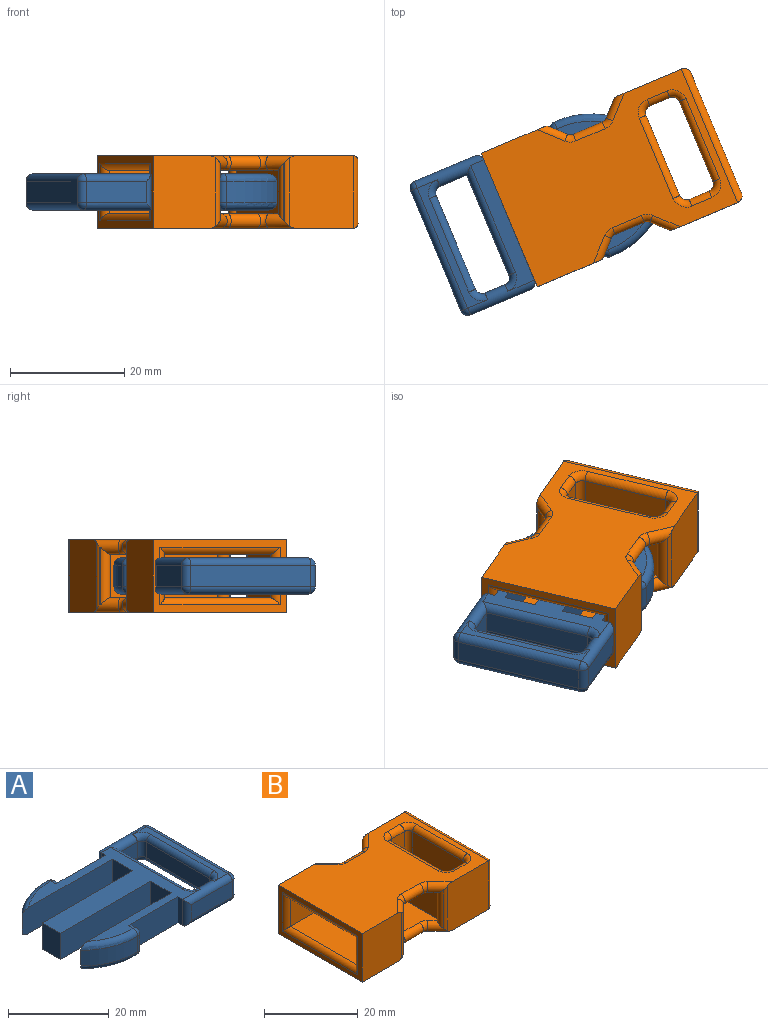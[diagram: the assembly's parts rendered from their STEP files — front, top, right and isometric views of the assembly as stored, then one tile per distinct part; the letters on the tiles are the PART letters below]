
ASSEMBLY  parts=2 mates=1
PART A: 67 faces, bbox 40.3x28.1x6.4 mm
  f0: plane 22.86x3.81mm, normal (0,0,1), area 31.8mm2, adj f28,f29,f33,f42,f43,f48
  f1: plane 22.86x3.81mm, normal (0,0,-1), area 31.8mm2, adj f31,f32,f36,f45,f46,f51
  f2: plane 17.78x3.81mm, normal (-1,0,0), area 67.7mm2, adj f27,f33,f36,f37
  f3: plane 3.81x3.81mm, normal (0,1,0), area 14.5mm2, adj f37,f39,f48,f51
  f4: plane 19.05x3.81mm, normal (1,0,0), area 72.6mm2, adj f23,f38,f39,f40
  f5: plane 6.35x1.27mm, normal (-1,0,0), area 8.1mm2, adj f6,f24,f25,f26
  f6: plane 13.97x6.35mm, normal (0,1,0), area 81.3mm2, adj f5,f7,f24,f25,f63,f66
  f7: plane 3.81x1.37mm, normal (1,0,0), area 5.2mm2, adj f6,f53,f63,f66
  f8: cylinder r=15.35mm len=11.48mm, axis (0,0,-1), area 48.4mm2, adj f9,f53,f61,f64
  f9: plane 25.4x6.35mm, normal (0,-1,0), area 160.3mm2, adj f8,f10,f24,f25,f61,f64
  f10: plane 6.35x5.72mm, normal (-1,0,0), area 36.3mm2, adj f9,f11,f24,f25
  f11: plane 25.4x6.35mm, normal (0,1,0), area 161.3mm2, adj f10,f12,f24,f25
  f12: plane 6.35x5.08mm, normal (-1,0,0), area 32.3mm2, adj f11,f13,f24,f25
  f13: plane 25.4x6.35mm, normal (0,-1,0), area 161.3mm2, adj f12,f14,f24,f25
  f14: plane 6.35x5.72mm, normal (-1,0,0), area 36.3mm2, adj f13,f15,f24,f25
  f15: plane 25.4x6.35mm, normal (0,1,0), area 160.3mm2, adj f14,f16,f24,f25,f55,f58
  f16: cylinder r=15.35mm len=11.48mm, axis (0,0,-1), area 48.4mm2, adj f15,f54,f55,f58
  f17: plane 3.81x1.37mm, normal (1,0,0), area 5.2mm2, adj f18,f54,f57,f60
  f18: plane 13.97x6.35mm, normal (0,-1,0), area 81.3mm2, adj f17,f19,f24,f25,f57,f60
  f19: plane 6.35x1.27mm, normal (-1,0,0), area 8.1mm2, adj f18,f24,f25,f52
  f20: plane 11.43x3.81mm, normal (0,-1,0), area 43.5mm2, adj f44,f48,f51,f52
  f21: plane 22.86x3.81mm, normal (1,0,0), area 87.1mm2, adj f30,f43,f44,f45
  f22: plane 11.43x3.81mm, normal (0,1,0), area 43.5mm2, adj f26,f28,f30,f31
  f23: plane 5.08x3.81mm, normal (0,-1,0), area 19.4mm2, adj f4,f27,f28,f31
  f24: plane 30.48x23.07mm, normal (0,0,1), area 285.7mm2, adj f5,f6,f9,f10,f11,f12,f13,f14
  f25: plane 30.48x23.07mm, normal (0,0,-1), area 285.7mm2, adj f5,f6,f9,f10,f11,f12,f13,f14
  f26: cylinder r=1.27mm len=6.35mm, axis (0,0,-1), area 10.8mm2, adj f5,f22,f28,f31
  f27: cylinder r=1.27mm len=3.81mm, axis (0,0,-1), area 7.6mm2, adj f2,f23,f29,f32
  f28: cylinder r=1.27mm len=12.7mm, axis (-1,0,0), area 35.5mm2, adj f0,f22,f23,f24,f26,f29,f34,f38
  f29: torus R=2.54mm, axis (0,0,1), area 5.4mm2, adj f0,f27,f28,f33
  f30: cylinder r=1.27mm len=3.81mm, axis (0,0,1), area 7.6mm2, adj f21,f22,f34,f35
  f31: cylinder r=1.27mm len=12.7mm, axis (-1,0,0), area 35.5mm2, adj f1,f22,f23,f25,f26,f32,f35,f40
  f32: torus R=2.54mm, axis (0,0,1), area 5.4mm2, adj f1,f27,f31,f36
  f33: cylinder r=1.27mm len=17.78mm, axis (0,1,0), area 35.5mm2, adj f0,f2,f29,f42
  f34: sphere r=1.27mm, area 2.5mm2, adj f28,f30,f43
  f35: sphere r=1.27mm, area 2.5mm2, adj f30,f31,f45
  f36: cylinder r=1.27mm len=17.78mm, axis (0,-1,0), area 35.5mm2, adj f1,f2,f32,f46
  f37: cylinder r=1.27mm len=3.81mm, axis (0,0,1), area 7.6mm2, adj f2,f3,f42,f46
  f38: cylinder r=1.27mm len=20.32mm, axis (0,-1,0), area 38.9mm2, adj f4,f24,f28,f41
  f39: cylinder r=1.27mm len=3.81mm, axis (0,0,-1), area 7.6mm2, adj f3,f4,f41,f47
  f40: cylinder r=1.27mm len=20.32mm, axis (0,1,0), area 38.9mm2, adj f4,f25,f31,f47
  f41: torus R=2.54mm, axis (0,0,1), area 5.4mm2, adj f24,f38,f39,f48
  f42: torus R=2.54mm, axis (0,0,1), area 5.4mm2, adj f0,f33,f37,f48
  f43: cylinder r=1.27mm len=22.86mm, axis (0,-1,0), area 45.6mm2, adj f0,f21,f34,f49
  f44: cylinder r=1.27mm len=3.81mm, axis (0,0,-1), area 7.6mm2, adj f20,f21,f49,f50
  f45: cylinder r=1.27mm len=22.86mm, axis (0,1,0), area 45.6mm2, adj f1,f21,f35,f50
  f46: torus R=2.54mm, axis (0,0,1), area 5.4mm2, adj f1,f36,f37,f51
  f47: torus R=2.54mm, axis (0,0,1), area 5.4mm2, adj f25,f39,f40,f51
  f48: cylinder r=1.27mm len=12.7mm, axis (1,0,0), area 32mm2, adj f0,f3,f20,f24,f41,f42,f49,f52
  f49: sphere r=1.27mm, area 2.5mm2, adj f43,f44,f48
  f50: sphere r=1.27mm, area 2.5mm2, adj f44,f45,f51
  f51: cylinder r=1.27mm len=12.7mm, axis (-1,0,0), area 32mm2, adj f1,f3,f20,f25,f46,f47,f50,f52
  f52: cylinder r=1.27mm len=6.35mm, axis (0,0,1), area 10.8mm2, adj f19,f20,f48,f51
  f53: cylinder r=1.27mm len=3.81mm, axis (0,0,-1), area 7.4mm2, adj f7,f8,f62,f65
  f54: cylinder r=1.27mm len=3.81mm, axis (0,0,-1), area 7.4mm2, adj f16,f17,f56,f59
  f55: torus R=14.08mm, axis (0,0,1), area 23.6mm2, adj f15,f16,f24,f56
  f56: sphere r=1.27mm, area 2.5mm2, adj f54,f55,f57
  f57: cylinder r=1.27mm len=1.37mm, axis (0,-1,0), area 2.7mm2, adj f17,f18,f24,f56
  f58: torus R=14.08mm, axis (0,0,1), area 23.6mm2, adj f15,f16,f25,f59
  f59: sphere r=1.27mm, area 2.5mm2, adj f54,f58,f60
  f60: cylinder r=1.27mm len=1.37mm, axis (0,1,0), area 2.7mm2, adj f17,f18,f25,f59
  f61: torus R=14.08mm, axis (0,0,1), area 23.6mm2, adj f8,f9,f24,f62
  f62: sphere r=1.27mm, area 2.5mm2, adj f53,f61,f63
  f63: cylinder r=1.27mm len=1.37mm, axis (0,-1,0), area 2.7mm2, adj f6,f7,f24,f62
  f64: torus R=14.08mm, axis (0,0,1), area 23.6mm2, adj f8,f9,f25,f65
  f65: sphere r=1.27mm, area 2.5mm2, adj f53,f64,f66
  f66: cylinder r=1.27mm len=1.37mm, axis (0,1,0), area 2.7mm2, adj f6,f7,f25,f65
PART B: 73 faces, bbox 39.4x27.2x12.7 mm
  f0: plane 15.24x10.16mm, normal (-1,0,0), area 154.8mm2, adj f61,f66,f69,f72
  f1: plane 10.16x3.81mm, normal (0,1,0), area 38.7mm2, adj f58,f67,f68,f72
  f2: plane 15.24x10.16mm, normal (1,0,0), area 154.8mm2, adj f53,f57,f58,f59
  f3: plane 12.7x11.92mm, normal (0,-1,0), area 151.1mm2, adj f10,f12,f13,f27,f29,f31
  f4: plane 10.16x0.08mm, normal (-0.71,-0.71,0), area 1.2mm2, adj f19,f21,f23,f24
  f5: plane 12.7x12.17mm, normal (0,-1,0), area 154.3mm2, adj f12,f13,f19,f23,f24,f52
  f6: plane 22.86x10.16mm, normal (1,0,0), area 232.3mm2, adj f49,f50,f51,f52
  f7: plane 12.7x12.17mm, normal (0,1,0), area 154.3mm2, adj f12,f13,f37,f41,f42,f49
  f8: plane 10.16x0.08mm, normal (-0.71,0.71,0), area 1.2mm2, adj f37,f39,f41,f42
  f9: plane 12.7x11.92mm, normal (0,1,0), area 151.1mm2, adj f10,f12,f13,f34,f36,f38
  f10: plane 25.4x12.7mm, normal (-1,0,0), area 90.3mm2, adj f3,f9,f12,f13,f45,f46,f47,f48
  f11: plane 10.16x3.81mm, normal (0,-1,0), area 38.7mm2, adj f53,f56,f60,f61
  f12: plane 38.1x25.4mm, normal (0,0,1), area 685.6mm2, adj f3,f5,f7,f9,f10,f19,f20,f22
  f13: plane 38.1x25.4mm, normal (0,0,-1), area 685.6mm2, adj f3,f5,f7,f9,f10,f23,f26,f28
  f14: plane 24.13x21.06mm, normal (0,0,1), area 455mm2, adj f15,f17,f18,f21,f23,f26,f28,f29
  f15: plane 10.65x7.62mm, normal (0,1,0), area 81.2mm2, adj f14,f16,f29,f48
  f16: plane 24.13x21.06mm, normal (0,0,-1), area 455mm2, adj f15,f17,f18,f19,f20,f21,f22,f25
  f17: plane 10.65x7.62mm, normal (0,-1,0), area 81.2mm2, adj f14,f16,f36,f45
  f18: plane 20.32x7.62mm, normal (-1,0,0), area 154.8mm2, adj f14,f16,f21,f39
  f19: cylinder r=1.27mm len=4.6mm, axis (0.71,-0.71,0), area 13.7mm2, adj f4,f5,f12,f16,f20,f21,f24
  f20: torus R=2.54mm, axis (0,0,-1), area 5.4mm2, adj f12,f16,f19,f22
  f21: cylinder r=1.27mm len=10.16mm, axis (0,0,1), area 21.2mm2, adj f4,f14,f16,f18,f19,f23
  f22: cylinder r=1.27mm len=5.55mm, axis (1,0,0), area 22.2mm2, adj f12,f16,f20,f25
  f23: cylinder r=1.27mm len=4.6mm, axis (-0.71,0.71,0), area 13.7mm2, adj f4,f5,f13,f14,f21,f24,f26
  f24: cylinder r=1.27mm len=11.96mm, axis (0,0,-1), area 11.1mm2, adj f4,f5,f19,f23
  f25: torus R=2.54mm, axis (0,0,-1), area 5.4mm2, adj f12,f16,f22,f27
  f26: torus R=2.54mm, axis (0,0,-1), area 5.4mm2, adj f13,f14,f23,f28
  f27: cylinder r=1.27mm len=4.6mm, axis (0.71,0.71,0), area 13.9mm2, adj f3,f12,f16,f25,f29
  f28: cylinder r=1.27mm len=5.55mm, axis (-1,0,0), area 22.2mm2, adj f13,f14,f26,f30
  f29: cylinder r=1.27mm len=11.96mm, axis (0,0,1), area 35.7mm2, adj f3,f14,f15,f16,f27,f31
  f30: torus R=2.54mm, axis (0,0,-1), area 5.4mm2, adj f13,f14,f28,f31
  f31: cylinder r=1.27mm len=4.6mm, axis (-0.71,-0.71,0), area 13.9mm2, adj f3,f13,f14,f29,f30
  f32: torus R=2.54mm, axis (0,0,-1), area 5.4mm2, adj f12,f16,f33,f34
  f33: cylinder r=1.27mm len=5.55mm, axis (-1,0,0), area 22.2mm2, adj f12,f16,f32,f35
  f34: cylinder r=1.27mm len=4.6mm, axis (-0.71,0.71,0), area 13.9mm2, adj f9,f12,f16,f32,f36
  f35: torus R=2.54mm, axis (0,0,-1), area 5.4mm2, adj f12,f16,f33,f37
  f36: cylinder r=1.27mm len=11.96mm, axis (0,0,-1), area 35.7mm2, adj f9,f14,f16,f17,f34,f38
  f37: cylinder r=1.27mm len=4.6mm, axis (-0.71,-0.71,0), area 13.7mm2, adj f7,f8,f12,f16,f35,f39,f41
  f38: cylinder r=1.27mm len=4.6mm, axis (0.71,-0.71,0), area 13.9mm2, adj f9,f13,f14,f36,f40
  f39: cylinder r=1.27mm len=10.16mm, axis (0,0,1), area 21.2mm2, adj f8,f14,f16,f18,f37,f42
  f40: torus R=2.54mm, axis (0,0,-1), area 5.4mm2, adj f13,f14,f38,f43
  f41: cylinder r=1.27mm len=11.96mm, axis (0,0,-1), area 11.1mm2, adj f7,f8,f37,f42
  f42: cylinder r=1.27mm len=4.6mm, axis (0.71,0.71,0), area 13.7mm2, adj f7,f8,f13,f14,f39,f41,f44
  f43: cylinder r=1.27mm len=5.55mm, axis (1,0,0), area 22.2mm2, adj f13,f14,f40,f44
  f44: torus R=2.54mm, axis (0,0,-1), area 5.4mm2, adj f13,f14,f42,f43
  f45: cylinder r=1.27mm len=10.16mm, axis (0,0,-1), area 17mm2, adj f10,f17,f46,f47
  f46: cylinder r=1.27mm len=22.86mm, axis (0,1,0), area 42.4mm2, adj f10,f16,f45,f48
  f47: cylinder r=1.27mm len=22.86mm, axis (0,-1,0), area 42.4mm2, adj f10,f14,f45,f48
  f48: cylinder r=1.27mm len=10.16mm, axis (0,0,1), area 17mm2, adj f10,f15,f46,f47
  f49: cylinder r=1.27mm len=12.7mm, axis (0,0,-1), area 23.5mm2, adj f6,f7,f50,f51
  f50: cylinder r=1.27mm len=25.4mm, axis (0,-1,0), area 48.8mm2, adj f6,f12,f49,f52
  f51: cylinder r=1.27mm len=25.4mm, axis (0,1,0), area 48.8mm2, adj f6,f13,f49,f52
  f52: cylinder r=1.27mm len=12.7mm, axis (0,0,1), area 23.5mm2, adj f5,f6,f50,f51
  f53: cylinder r=1.27mm len=10.16mm, axis (0,0,1), area 20.3mm2, adj f2,f11,f54,f55
  f54: torus R=2.54mm, axis (0,0,1), area 5.4mm2, adj f12,f53,f56,f57
  f55: torus R=2.54mm, axis (0,0,1), area 5.4mm2, adj f13,f53,f59,f60
  f56: cylinder r=1.27mm len=3.81mm, axis (-1,0,0), area 7.6mm2, adj f11,f12,f54,f62
  f57: cylinder r=1.27mm len=15.24mm, axis (0,-1,0), area 30.4mm2, adj f2,f12,f54,f63
  f58: cylinder r=1.27mm len=10.16mm, axis (0,0,-1), area 20.3mm2, adj f1,f2,f63,f64
  f59: cylinder r=1.27mm len=15.24mm, axis (0,1,0), area 30.4mm2, adj f2,f13,f55,f64
  f60: cylinder r=1.27mm len=3.81mm, axis (1,0,0), area 7.6mm2, adj f11,f13,f55,f65
  f61: cylinder r=1.27mm len=10.16mm, axis (0,0,-1), area 20.3mm2, adj f0,f11,f62,f65
  f62: torus R=2.54mm, axis (0,0,1), area 5.4mm2, adj f12,f56,f61,f66
  f63: torus R=2.54mm, axis (0,0,1), area 5.4mm2, adj f12,f57,f58,f67
  f64: torus R=2.54mm, axis (0,0,1), area 5.4mm2, adj f13,f58,f59,f68
  f65: torus R=2.54mm, axis (0,0,1), area 5.4mm2, adj f13,f60,f61,f69
  f66: cylinder r=1.27mm len=15.24mm, axis (0,1,0), area 30.4mm2, adj f0,f12,f62,f70
  f67: cylinder r=1.27mm len=3.81mm, axis (1,0,0), area 7.6mm2, adj f1,f12,f63,f70
  f68: cylinder r=1.27mm len=3.81mm, axis (-1,0,0), area 7.6mm2, adj f1,f13,f64,f71
  f69: cylinder r=1.27mm len=15.24mm, axis (0,-1,0), area 30.4mm2, adj f0,f13,f65,f71
  f70: torus R=2.54mm, axis (0,0,1), area 5.4mm2, adj f12,f66,f67,f72
  f71: torus R=2.54mm, axis (0,0,1), area 5.4mm2, adj f13,f68,f69,f72
  f72: cylinder r=1.27mm len=10.16mm, axis (0,0,1), area 20.3mm2, adj f0,f1,f70,f71
PLACE A rot(axis=(0.2,-0.98,0),180deg) t=(-30.34,12.28,0.77)mm
PLACE B rot(axis=(0,0,1),22.8deg) t=(5.95,27.53,-8.76)mm
MATE fastened A.f12 <-> B.f18  axis (0.92,0.39,0) through (-0.49,24.82,-2.41)mm
